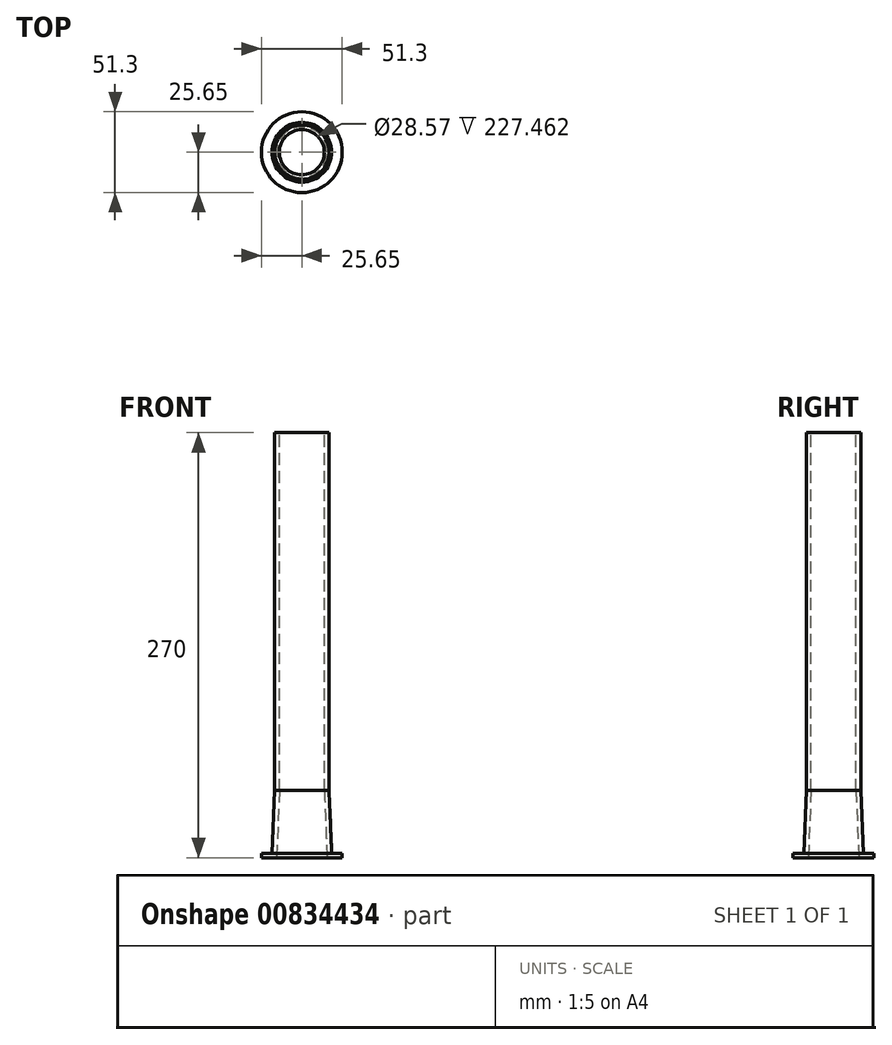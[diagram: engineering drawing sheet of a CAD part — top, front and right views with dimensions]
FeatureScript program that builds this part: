
annotation { "Feature Type Name" : "Feature", "Feature Type Description" : "" }
export const myFeature = defineFeature(function(context is Context, id is Id, definition is map)
    precondition{}
    {
        {
            var Q0;
            Q0=qCreatedBy(makeId("Front.planeOp"),FACE);
            var sketch = newSketch(context, id + "F0", { "sketchPlane" : qUnion([Q0])});
            skLineSegment(sketch, "E0", {"start": v(0, 0) * mm, "end": v(0, -1000) * mm});
            skPoint(sketch, "E1", {"position": v(0, -270) * mm});
            skLineSegment(sketch, "E2", {"start": v(0, 0) * mm, "end": v(14.29, 0) * mm});
            skLineSegment(sketch, "E3", {"start": v(14.29, 0) * mm, "end": v(17.29, 0) * mm});
            skLineSegment(sketch, "E4", {"start": v(17.29, 0) * mm, "end": v(17.29, -227.37) * mm});
            skLineSegment(sketch, "E5", {"start": v(14.29, 0) * mm, "end": v(14.29, -227.46) * mm});
            skPoint(sketch, "E6.orphan", {"position": v(0, -260) * mm});
            skLineSegment(sketch, "E7", {"start": v(16.05, -270) * mm, "end": v(19.05, -270) * mm});
            skLineSegment(sketch, "E8.trimOffspring", {"start": v(16.05, -270) * mm, "end": v(25.65, -270) * mm});
            skLineSegment(sketch, "E9", {"start": v(17.29, -227.37) * mm, "end": v(18.93, -267.09) * mm});
            skLineSegment(sketch, "E10", {"start": v(14.29, -227.46) * mm, "end": v(16.05, -270) * mm});
            skLineSegment(sketch, "E11", {"start": v(25.65, -270) * mm, "end": v(25.65, -267.09) * mm});
            skLineSegment(sketch, "E12", {"start": v(25.65, -267.09) * mm, "end": v(18.93, -267.09) * mm});
            skLineSegment(sketch, "E13", {"start": v(0, -270) * mm, "end": v(-25.65, -270) * mm});
            skPoint(sketch, "E14", {"position": v(0, -330) * mm});
            skLineSegment(sketch, "E15", {"start": v(25.65, -270) * mm, "end": v(25.65, -665) * mm});
            skSolve(sketch);
        }
        {
            var Q0;
            Q0=makeQuery(id+"F0.imprint","IMPRINT",FACE,{"disambiguationData":[TD([[makeQuery(id+"F0.imprint","IMPRINT",EDGE,{"derivedFrom":sQuery(id+"F0.wireOp",EDGE,"E3")}),-1.0]])]});
            var Q1;
            Q1=sQuery(id+"F0.wireOp",EDGE,"E0");
            revolve(context, id + "F1", {"surfaceOperationType" : NewSurfaceOperationType.NEW, "entities" : qUnion([Q0]), "axis" : qUnion([Q1]), "revolveType" : RevolveType.FULL});
        }
    });
